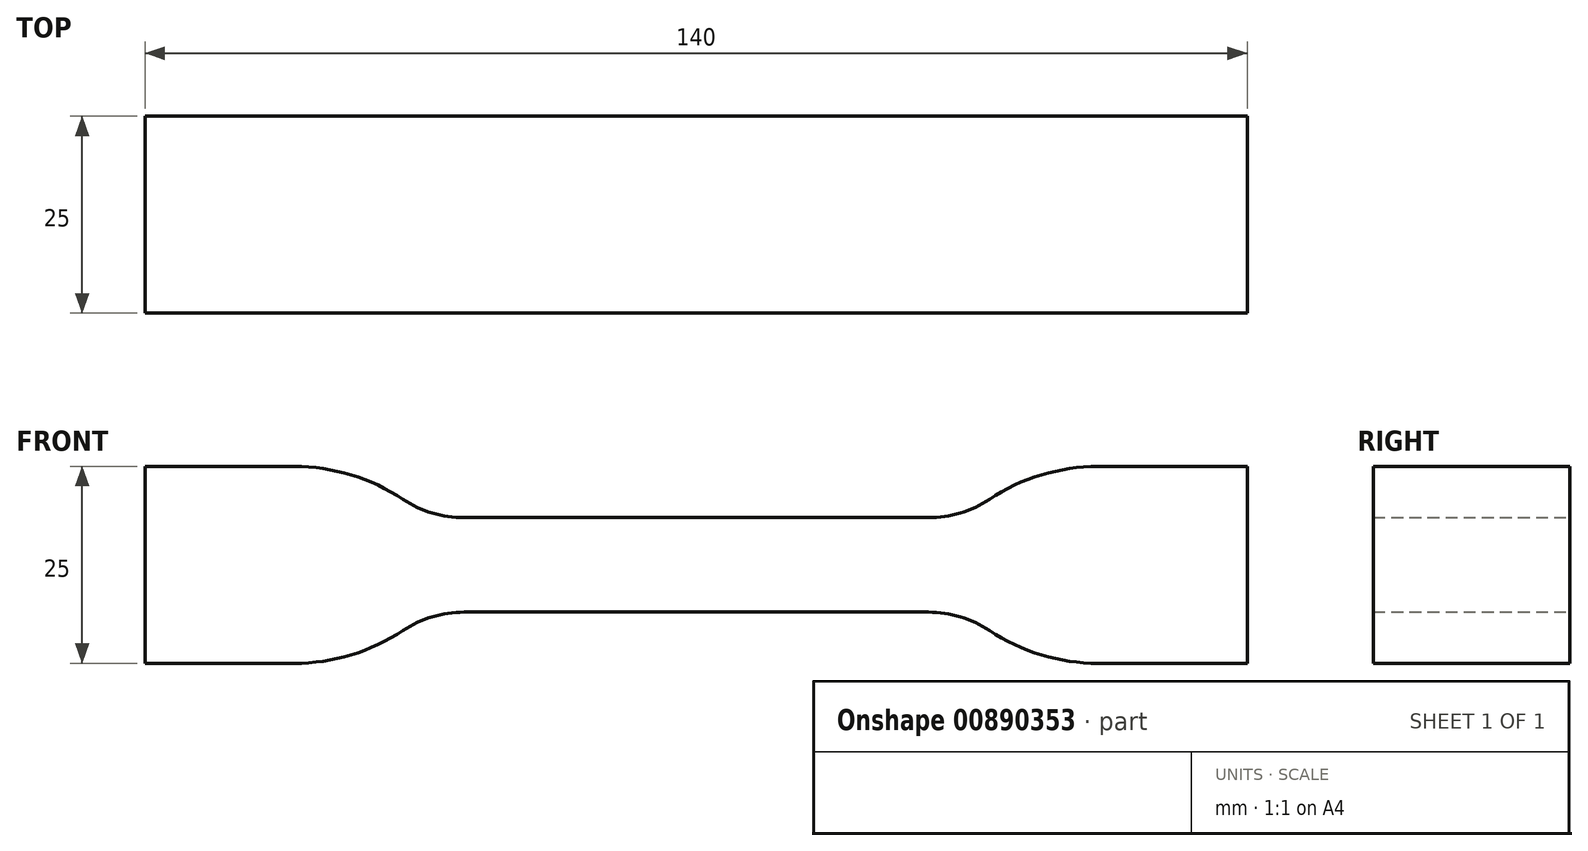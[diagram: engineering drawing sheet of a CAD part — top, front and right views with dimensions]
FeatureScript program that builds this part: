
annotation { "Feature Type Name" : "Feature", "Feature Type Description" : "" }
export const myFeature = defineFeature(function(context is Context, id is Id, definition is map)
    precondition{}
    {
        {
            var Q0;
            Q0=qCreatedBy(makeId("Front.planeOp"),FACE);
            var sketch = newSketch(context, id + "F0", { "sketchPlane" : qUnion([Q0])});
            skLineSegment(sketch, "E0.bottom", {"start": v(29.5, -6) * mm, "end": v(-29.5, -6) * mm});
            skLineSegment(sketch, "E0.top", {"start": v(29.5, 6) * mm, "end": v(-29.5, 6) * mm});
            skPoint(sketch, "E0.middle", {"position": v(0, 0) * mm});
            skArc(sketch, "E1", {"start": v(-29.5, 6) * mm, "mid": v(-33.54, 6.6) * mm, "end": v(-37.24, 8.33) * mm});
            skArc(sketch, "E2", {"start": v(-37.24, 8.33) * mm, "mid": v(-43.84, 11.44) * mm, "end": v(-51.06, 12.5) * mm});
            skLineSegment(sketch, "E3", {"start": v(-51.06, 12.5) * mm, "end": v(-70, 12.5) * mm});
            skLineSegment(sketch, "E4", {"start": v(-70, 12.5) * mm, "end": v(-70, 0) * mm});
            skLineSegment(sketch, "E5.MirrorCS", {"start": v(-70, -12.5) * mm, "end": v(-70, 0) * mm});
            skLineSegment(sketch, "E6.MirrorCS", {"start": v(-51.06, -12.5) * mm, "end": v(-70, -12.5) * mm});
            skArc(sketch, "E7.MirrorCS", {"start": v(-37.24, -8.33) * mm, "mid": v(-43.84, -11.44) * mm, "end": v(-51.06, -12.5) * mm});
            skArc(sketch, "E8.MirrorCS", {"start": v(-29.5, -6) * mm, "mid": v(-33.54, -6.6) * mm, "end": v(-37.24, -8.33) * mm});
            skLineSegment(sketch, "E9.MirrorCS", {"start": v(51.06, 12.5) * mm, "end": v(70, 12.5) * mm});
            skLineSegment(sketch, "E10.MirrorCS", {"start": v(51.06, -12.5) * mm, "end": v(70, -12.5) * mm});
            skLineSegment(sketch, "E11.MirrorCS", {"start": v(70, -12.5) * mm, "end": v(70, 0) * mm});
            skLineSegment(sketch, "E12.MirrorCS", {"start": v(70, 12.5) * mm, "end": v(70, 0) * mm});
            skArc(sketch, "E13.MirrorCS", {"start": v(37.24, 8.33) * mm, "mid": v(43.84, 11.44) * mm, "end": v(51.06, 12.5) * mm});
            skArc(sketch, "E14.MirrorCS", {"start": v(37.24, -8.33) * mm, "mid": v(43.84, -11.44) * mm, "end": v(51.06, -12.5) * mm});
            skArc(sketch, "E15.MirrorCS", {"start": v(29.5, -6) * mm, "mid": v(33.54, -6.6) * mm, "end": v(37.24, -8.33) * mm});
            skArc(sketch, "E16.MirrorCS", {"start": v(29.5, 6) * mm, "mid": v(33.54, 6.6) * mm, "end": v(37.24, 8.33) * mm});
            skSolve(sketch);
        }
        {
            var Q0;
            Q0=makeQuery(id+"F0.imprint","IMPRINT",FACE,{"disambiguationData":[TD([[makeQuery(id+"F0.imprint","IMPRINT",EDGE,{"derivedFrom":sQuery(id+"F0.wireOp",EDGE,"E0.bottom")}),-1.0]])]});
            extrude(context, id + "F1", {"entities" : qUnion([Q0]), "depth" : 25 * mm, "offsetDistance" : 25 * mm});
        }
    });
